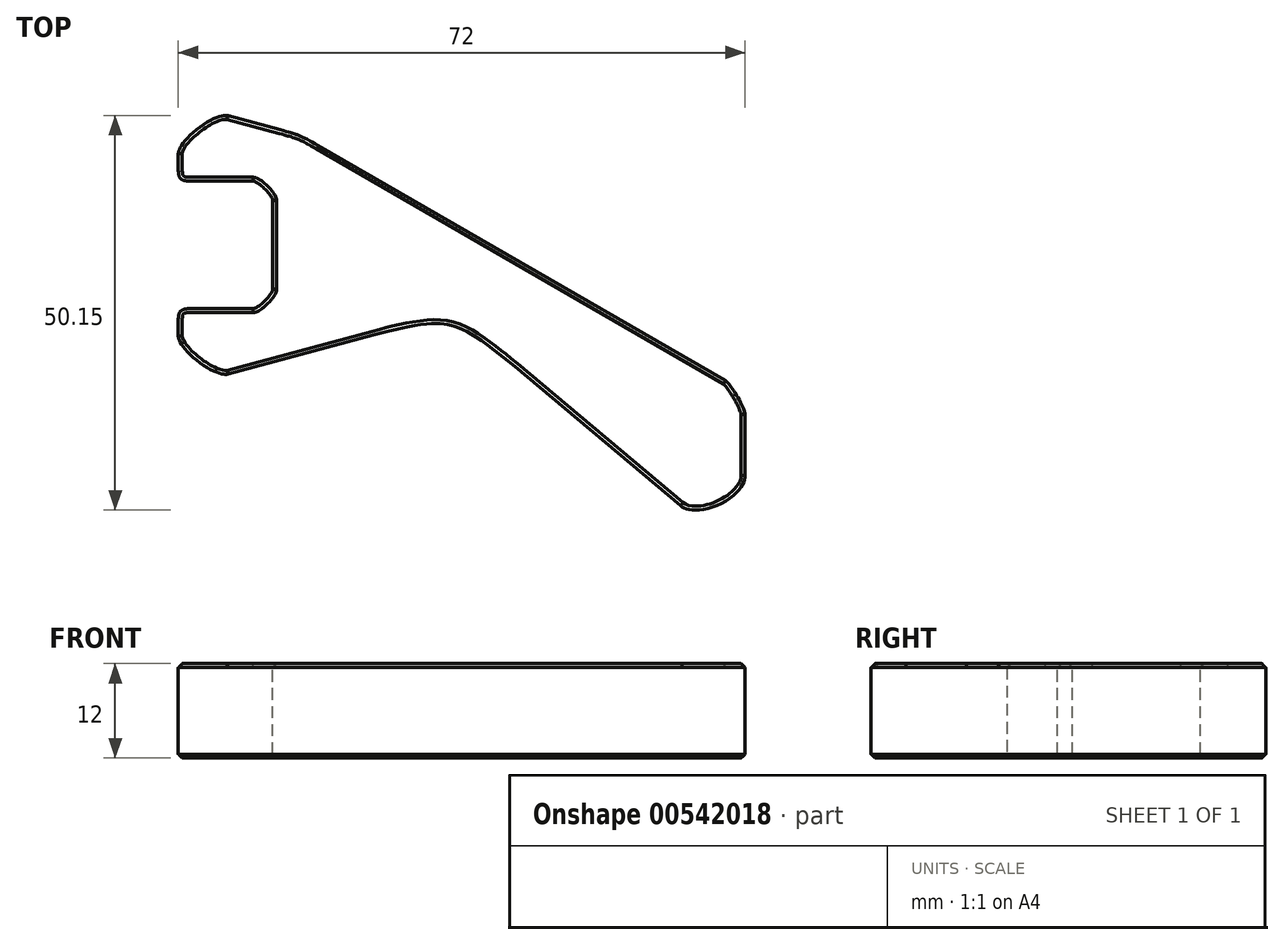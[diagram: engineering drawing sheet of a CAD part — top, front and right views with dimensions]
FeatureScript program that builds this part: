
annotation { "Feature Type Name" : "Feature", "Feature Type Description" : "" }
export const myFeature = defineFeature(function(context is Context, id is Id, definition is map)
    precondition{}
    {
        {
            var Q0;
            Q0=qCreatedBy(makeId("Top.planeOp"),FACE);
            var sketch = newSketch(context, id + "F0", { "sketchPlane" : qUnion([Q0])});
            skLineSegment(sketch, "E0", {"start": v(-12, 0) * mm, "end": v(0, 0) * mm});
            skLineSegment(sketch, "E1", {"start": v(0, 0) * mm, "end": v(0, 16.2) * mm});
            skLineSegment(sketch, "E2", {"start": v(0, 16.2) * mm, "end": v(-12, 16.2) * mm});
            skLineSegment(sketch, "E3", {"start": v(-12, 16.2) * mm, "end": v(-12, 26.2) * mm});
            skLineSegment(sketch, "E4", {"start": v(-12, 26.2) * mm, "end": v(3.45, 22.06) * mm});
            skLineSegment(sketch, "E5", {"start": v(3.45, 22.06) * mm, "end": v(60, -10.59) * mm});
            skLineSegment(sketch, "E6", {"start": v(60, -10.59) * mm, "end": v(60, -31.92) * mm});
            skLineSegment(sketch, "E7", {"start": v(60, -31.92) * mm, "end": v(22.77, -0.68) * mm});
            skLineSegment(sketch, "E8", {"start": v(22.77, -0.68) * mm, "end": v(-12, -10) * mm});
            skLineSegment(sketch, "E9", {"start": v(-12, -10) * mm, "end": v(-12, 0) * mm});
            skSolve(sketch);
        }
        {
            var Q0;
            Q0=makeQuery(id+"F0.imprint","IMPRINT",FACE,{"disambiguationData":[TD([[makeQuery(id+"F0.imprint","IMPRINT",EDGE,{"derivedFrom":sQuery(id+"F0.wireOp",EDGE,"E0")}),-1.0]])]});
            extrude(context, id + "F1", {"entities" : qUnion([Q0]), "depth" : 12 * mm, "offsetDistance" : 25 * mm, "symmetric" : true});
        }
        {
            var Q0;
            Q0=makeQuery(id+"F1.opExtrude","SWEPT_EDGE",EDGE,{"disambiguationData":[OSD([sQuery(id+"F0.wireOp",EDGE,"E1"),sQuery(id+"F0.wireOp",EDGE,"E2")])]});
            var Q1;
            Q1=makeQuery(id+"F1.opExtrude","SWEPT_EDGE",EDGE,{"disambiguationData":[OSD([sQuery(id+"F0.wireOp",EDGE,"E0"),sQuery(id+"F0.wireOp",EDGE,"E1")])]});
            fillet(context, id + "F2", {"entities" : qUnion([Q0, Q1]), "radius" : 2.5 * mm, "tangentPropagation" : true, "rho" : .2, "crossSection" : FilletCrossSection.CONIC, "allowEdgeOverflow" : false});
        }
        {
            var Q0;
            Q0=makeQuery(id+"F1.opExtrude","SWEPT_EDGE",EDGE,{"disambiguationData":[OSD([sQuery(id+"F0.wireOp",EDGE,"E7"),sQuery(id+"F0.wireOp",EDGE,"E8")])]});
            var Q1;
            Q1=makeQuery(id+"F1.opExtrude","SWEPT_EDGE",EDGE,{"disambiguationData":[OSD([sQuery(id+"F0.wireOp",EDGE,"E4"),sQuery(id+"F0.wireOp",EDGE,"E5")])]});
            fillet(context, id + "F3", {"entities" : qUnion([Q0, Q1]), "radius" : 20 * mm, "tangentPropagation" : true, "rho" : .7, "crossSection" : FilletCrossSection.CONIC, "allowEdgeOverflow" : false});
        }
        {
            var Q0;
            Q0=makeQuery(id+"F1.opExtrude","SWEPT_EDGE",EDGE,{"disambiguationData":[OSD([sQuery(id+"F0.wireOp",EDGE,"E2"),sQuery(id+"F0.wireOp",EDGE,"E3")])]});
            var Q1;
            Q1=makeQuery(id+"F1.opExtrude","SWEPT_EDGE",EDGE,{"disambiguationData":[OSD([sQuery(id+"F0.wireOp",EDGE,"E0"),sQuery(id+"F0.wireOp",EDGE,"E9")])]});
            fillet(context, id + "F4", {"entities" : qUnion([Q0, Q1]), "radius" : 1.5 * mm, "tangentPropagation" : true, "rho" : .6, "crossSection" : FilletCrossSection.CONIC, "allowEdgeOverflow" : false});
        }
        {
            var Q0;
            Q0=makeQuery(id+"F1.opExtrude","SWEPT_EDGE",EDGE,{"disambiguationData":[OSD([sQuery(id+"F0.wireOp",EDGE,"E3"),sQuery(id+"F0.wireOp",EDGE,"E4")])]});
            var Q1;
            Q1=makeQuery(id+"F1.opExtrude","SWEPT_EDGE",EDGE,{"disambiguationData":[OSD([sQuery(id+"F0.wireOp",EDGE,"E8"),sQuery(id+"F0.wireOp",EDGE,"E9")])]});
            var Q2;
            Q2=makeQuery(id+"F1.opExtrude","SWEPT_EDGE",EDGE,{"disambiguationData":[OSD([sQuery(id+"F0.wireOp",EDGE,"E6"),sQuery(id+"F0.wireOp",EDGE,"E7")])]});
            var Q3;
            Q3=makeQuery(id+"F1.opExtrude","SWEPT_EDGE",EDGE,{"disambiguationData":[OSD([sQuery(id+"F0.wireOp",EDGE,"E5"),sQuery(id+"F0.wireOp",EDGE,"E6")])]});
            fillet(context, id + "F5", {"entities" : qUnion([Q0, Q1, Q2, Q3]), "radius" : 5 * mm, "tangentPropagation" : true, "rho" : .2, "crossSection" : FilletCrossSection.CONIC, "allowEdgeOverflow" : false});
        }
        {
            var Q0;
            Q0=makeQuery(id+"F1.opExtrude","CAP_FACE",FACE,{"disambiguationData":[OSD([sQuery(id+"F0.wireOp",EDGE,"E0"),sQuery(id+"F0.wireOp",EDGE,"E1"),sQuery(id+"F0.wireOp",EDGE,"E2"),sQuery(id+"F0.wireOp",EDGE,"E3"),sQuery(id+"F0.wireOp",EDGE,"E4"),sQuery(id+"F0.wireOp",EDGE,"E5"),sQuery(id+"F0.wireOp",EDGE,"E6"),sQuery(id+"F0.wireOp",EDGE,"E7"),sQuery(id+"F0.wireOp",EDGE,"E8"),sQuery(id+"F0.wireOp",EDGE,"E9")])],"isStart":false});
            var Q1;
            Q1=makeQuery(id+"F1.opExtrude","CAP_FACE",FACE,{"disambiguationData":[OSD([sQuery(id+"F0.wireOp",EDGE,"E0"),sQuery(id+"F0.wireOp",EDGE,"E1"),sQuery(id+"F0.wireOp",EDGE,"E2"),sQuery(id+"F0.wireOp",EDGE,"E3"),sQuery(id+"F0.wireOp",EDGE,"E4"),sQuery(id+"F0.wireOp",EDGE,"E5"),sQuery(id+"F0.wireOp",EDGE,"E6"),sQuery(id+"F0.wireOp",EDGE,"E7"),sQuery(id+"F0.wireOp",EDGE,"E8"),sQuery(id+"F0.wireOp",EDGE,"E9")])],"isStart":true});
            chamfer(context, id + "F6", {"entities" : qUnion([Q0, Q1]), "width" : .5 * mm, "tangentPropagation" : true});
        }
    });
